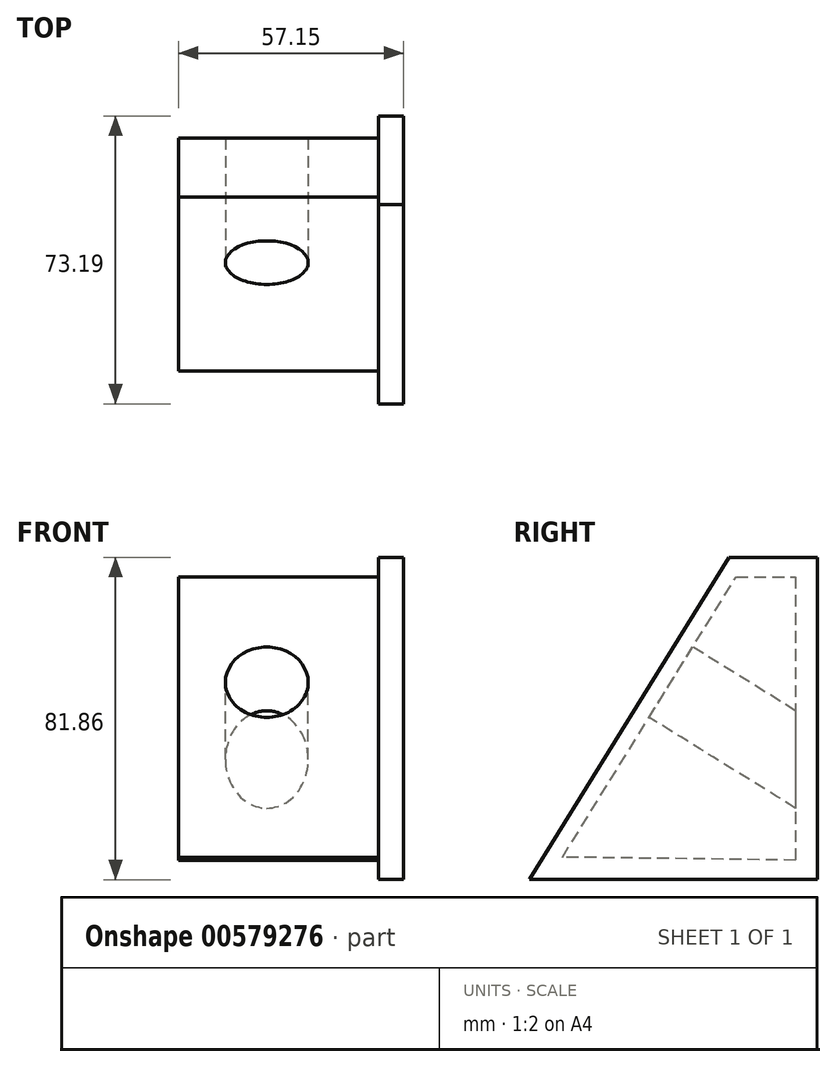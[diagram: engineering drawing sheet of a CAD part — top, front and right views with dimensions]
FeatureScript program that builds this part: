
annotation { "Feature Type Name" : "Feature", "Feature Type Description" : "" }
export const myFeature = defineFeature(function(context is Context, id is Id, definition is map)
    precondition{}
    {
        {
            var Q0;
            Q0=qCreatedBy(makeId("Right.planeOp"),FACE);
            var sketch = newSketch(context, id + "F0", { "sketchPlane" : qUnion([Q0])});
            skLineSegment(sketch, "E0", {"start": v(41.39, 46.37) * mm, "end": v(41.39, -35.49) * mm});
            skLineSegment(sketch, "E1", {"start": v(41.39, -35.49) * mm, "end": v(-31.8, -35.49) * mm});
            skLineSegment(sketch, "E2", {"start": v(-31.8, -35.49) * mm, "end": v(18.9, 46.37) * mm});
            skLineSegment(sketch, "E3", {"start": v(18.9, 46.37) * mm, "end": v(41.39, 46.37) * mm});
            skSolve(sketch);
        }
        {
            var Q0;
            Q0=makeQuery(id+"F0.imprint","IMPRINT",FACE,{"disambiguationData":[TD([[makeQuery(id+"F0.imprint","IMPRINT",EDGE,{"derivedFrom":sQuery(id+"F0.wireOp",EDGE,"E0")}),-1.0]])]});
            extrude(context, id + "F1", {"entities" : qUnion([Q0]), "depth" : 6.35 * mm, "offsetDistance" : 25.4 * mm});
        }
        {
            var Q0;
            Q0=makeQuery(id+"F1.opExtrude","CAP_FACE",FACE,{"disambiguationData":[OSD([sQuery(id+"F0.wireOp",EDGE,"E0"),sQuery(id+"F0.wireOp",EDGE,"E1"),sQuery(id+"F0.wireOp",EDGE,"E2"),sQuery(id+"F0.wireOp",EDGE,"E3")])],"isStart":true});
            var sketch = newSketch(context, id + "F2", { "sketchPlane" : qUnion([Q0])});
            skLineSegment(sketch, "E4", {"start": v(23.42, -29.79) * mm, "end": v(-20.72, 41.47) * mm});
            skLineSegment(sketch, "E5", {"start": v(-20.72, 41.47) * mm, "end": v(-35.81, 41.47) * mm});
            skLineSegment(sketch, "E6", {"start": v(-35.81, 41.47) * mm, "end": v(-35.81, -30.55) * mm});
            skLineSegment(sketch, "E7", {"start": v(-35.81, -30.55) * mm, "end": v(23.42, -29.79) * mm});
            skSolve(sketch);
        }
        {
            var Q0;
            Q0=makeQuery(id+"F2.imprint","IMPRINT",FACE,{"disambiguationData":[TD([[makeQuery(id+"F2.imprint","IMPRINT",EDGE,{"derivedFrom":sQuery(id+"F2.wireOp",EDGE,"E4")}),1.0]])]});
            extrude(context, id + "F3", {"entities" : qUnion([Q0]), "operationType" : NewBodyOperationType.ADD, "depth" : 50.8 * mm, "offsetDistance" : 25.4 * mm});
        }
        {
            var Q0;
            Q0=makeQuery(id+"F3.opExtrude","SWEPT_FACE",FACE,{"disambiguationData":[OSD([sQuery(id+"F2.wireOp",EDGE,"E4")])]});
            var sketch = newSketch(context, id + "F4", { "sketchPlane" : qUnion([Q0])});
            skCircle(sketch, "E8", {"center": v(-28.4, 14.64) * mm, "radius": 10.52 * mm});
            skSolve(sketch);
        }
        {
            var Q0;
            Q0=makeQuery(id+"F4.imprint","IMPRINT",FACE,{"disambiguationData":[TD([[makeQuery(id+"F4.imprint","IMPRINT",EDGE,{"derivedFrom":sQuery(id+"F4.wireOp",EDGE,"E8")}),1.0]])]});
            extrude(context, id + "F5", {"entities" : qUnion([Q0]), "operationType" : NewBodyOperationType.REMOVE, "oppositeDirection" : true, "depth" : 83.82 * mm, "offsetDistance" : 25.4 * mm});
        }
    });
